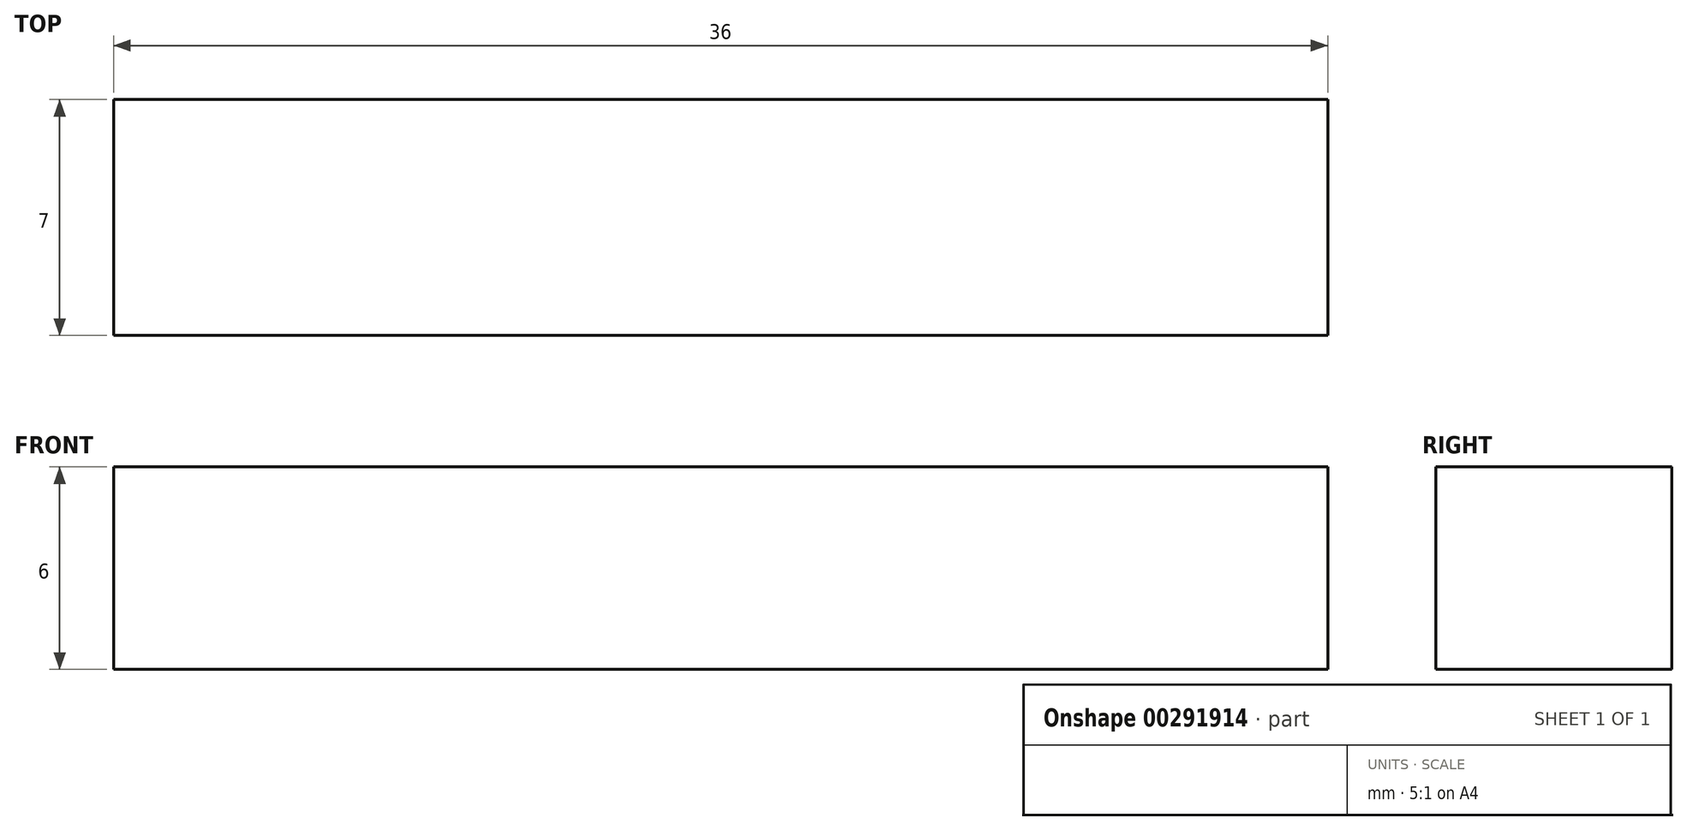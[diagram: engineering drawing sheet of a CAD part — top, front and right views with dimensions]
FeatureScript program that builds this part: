
annotation { "Feature Type Name" : "Feature", "Feature Type Description" : "" }
export const myFeature = defineFeature(function(context is Context, id is Id, definition is map)
    precondition{}
    {
        {
            var Q0;
            Q0=qCreatedBy(makeId("Front.planeOp"),FACE);
            var sketch = newSketch(context, id + "F0", { "sketchPlane" : qUnion([Q0])});
            skLineSegment(sketch, "E0", {"start": v(0, 3) * mm, "end": v(18, 3) * mm});
            skLineSegment(sketch, "E1", {"start": v(18, 0) * mm, "end": v(18, 3) * mm});
            skLineSegment(sketch, "E2.MirrorCS", {"start": v(0, 3) * mm, "end": v(-18, 3) * mm});
            skLineSegment(sketch, "E3.MirrorCS", {"start": v(-18, 0) * mm, "end": v(-18, 3) * mm});
            skLineSegment(sketch, "E4.MirrorCS", {"start": v(-18, 0) * mm, "end": v(-18, -3) * mm});
            skLineSegment(sketch, "E5.MirrorCS", {"start": v(18, 0) * mm, "end": v(18, -3) * mm});
            skLineSegment(sketch, "E6.MirrorCS", {"start": v(0, -3) * mm, "end": v(-18, -3) * mm});
            skLineSegment(sketch, "E7.MirrorCS", {"start": v(0, -3) * mm, "end": v(18, -3) * mm});
            skSolve(sketch);
        }
        {
            var Q0;
            Q0 = qSketchRegion(id + "F0", true);
            extrude(context, id + "F1", {"entities" : qUnion([Q0]), "endBound" : BoundingType.SYMMETRIC, "depth" : 7 * mm});
        }
    });
